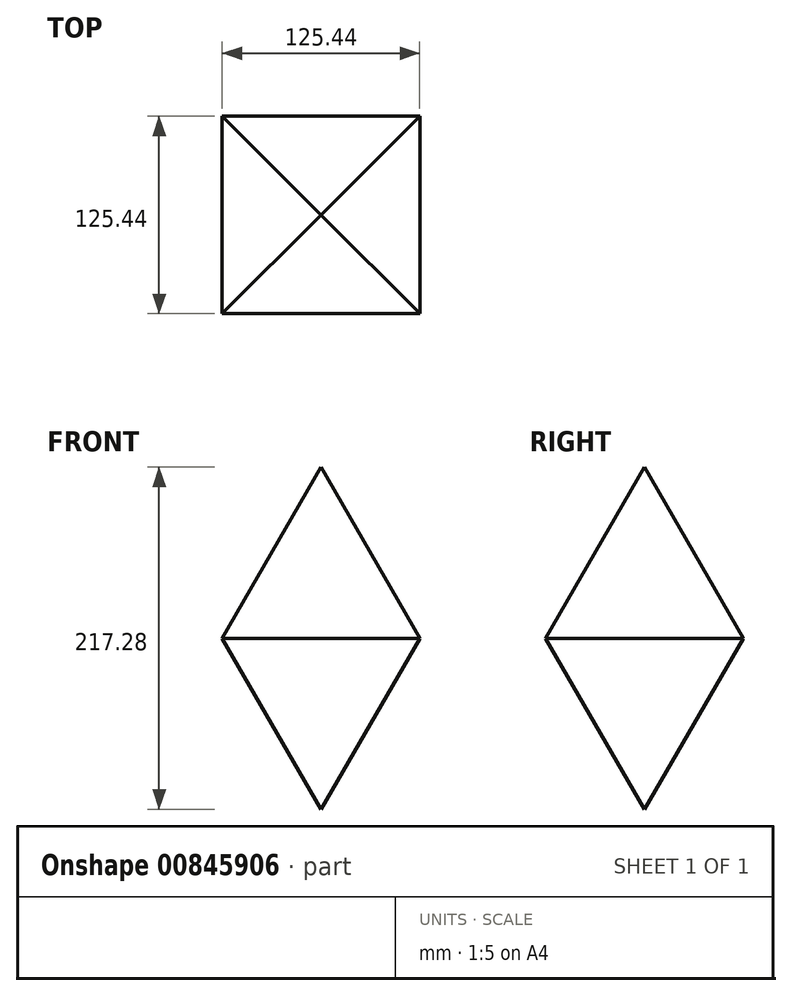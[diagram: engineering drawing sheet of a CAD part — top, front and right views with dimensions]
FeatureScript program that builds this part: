
annotation { "Feature Type Name" : "Feature", "Feature Type Description" : "" }
export const myFeature = defineFeature(function(context is Context, id is Id, definition is map)
    precondition{}
    {
        {
            var Q0;
            Q0=qCreatedBy(makeId("Top.planeOp"),FACE);
            var sketch = newSketch(context, id + "F0", { "sketchPlane" : qUnion([Q0])});
            skLineSegment(sketch, "E0.bottom", {"start": v(62.72, -62.72) * mm, "end": v(-62.72, -62.72) * mm});
            skLineSegment(sketch, "E0.top", {"start": v(62.72, 62.72) * mm, "end": v(-62.72, 62.72) * mm});
            skLineSegment(sketch, "E0.left", {"start": v(62.72, -62.72) * mm, "end": v(62.72, 62.72) * mm});
            skLineSegment(sketch, "E0.right", {"start": v(-62.72, -62.72) * mm, "end": v(-62.72, 62.72) * mm});
            skPoint(sketch, "E0.middle", {"position": v(0, 0) * mm});
            skSolve(sketch);
        }
        {
            var Q0;
            Q0=makeQuery(id+"F0.imprint","IMPRINT",FACE,{"disambiguationData":[TD([[makeQuery(id+"F0.imprint","IMPRINT",EDGE,{"derivedFrom":sQuery(id+"F0.wireOp",EDGE,"E0.bottom")}),-1.0]])]});
            extrude(context, id + "F1", {"entities" : qUnion([Q0]), "depth" : 109.22 * mm, "offsetDistance" : 25.4 * mm, "hasDraft" : true, "draftAngle" : 30 * degree, "draftPullDirection" : true, "hasSecondDirection" : true, "secondDirectionOppositeDirection" : true, "secondDirectionDepth" : 131.57 * mm, "hasSecondDirectionDraft" : true, "secondDirectionDraftAngle" : 30 * degree, "secondDirectionDraftPullDirection" : true});
        }
    });
